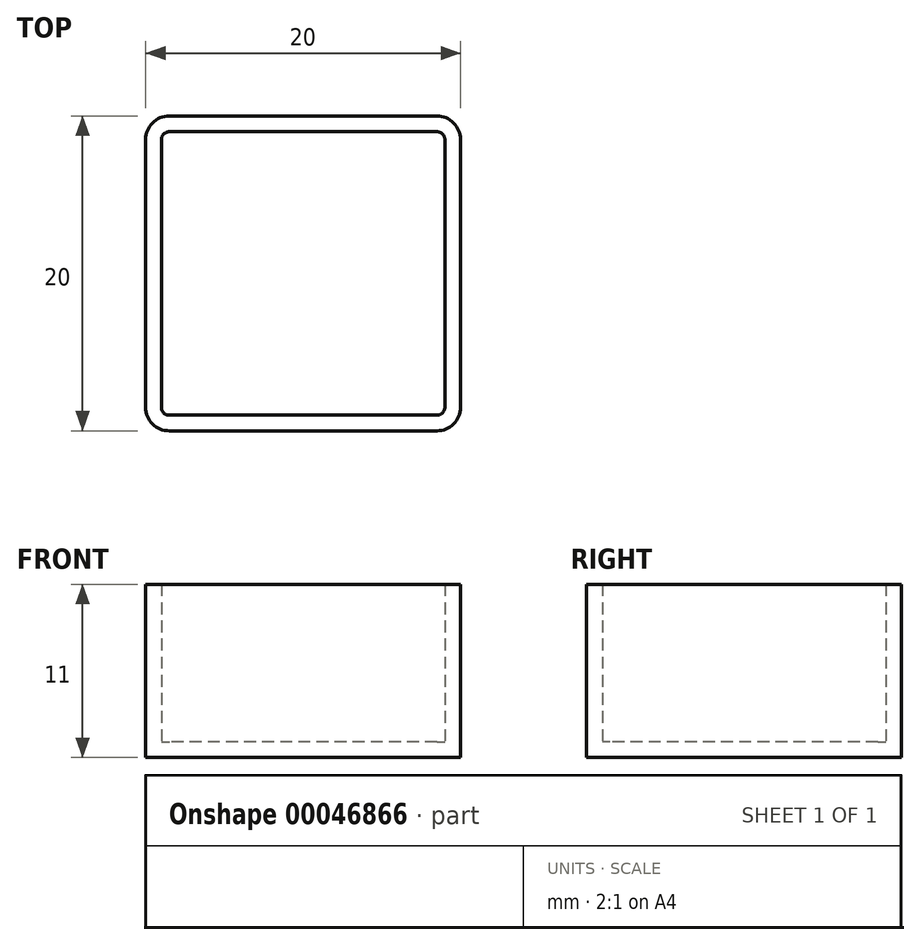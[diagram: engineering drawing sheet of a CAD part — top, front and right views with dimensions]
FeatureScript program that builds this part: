
annotation { "Feature Type Name" : "Feature", "Feature Type Description" : "" }
export const myFeature = defineFeature(function(context is Context, id is Id, definition is map)
    precondition{}
    {
        {
            var Q0;
            Q0=qCreatedBy(makeId("Top.planeOp"),FACE);
            var sketch = newSketch(context, id + "F0", { "sketchPlane" : qUnion([Q0])});
            skLineSegment(sketch, "E0.rect.bottom", {"start": v(10, 10) * mm, "end": v(-10, 10) * mm});
            skLineSegment(sketch, "E0.rect.top", {"start": v(10, -10) * mm, "end": v(-10, -10) * mm});
            skLineSegment(sketch, "E0.rect.left", {"start": v(10, 10) * mm, "end": v(10, -10) * mm});
            skLineSegment(sketch, "E0.rect.right", {"start": v(-10, 10) * mm, "end": v(-10, -10) * mm});
            skPoint(sketch, "E0.rect.middle", {"position": v(0, 0) * mm});
            skSolve(sketch);
        }
        {
            var Q0;
            Q0=makeQuery(id+"F0.imprint","IMPRINT",FACE,{"disambiguationData":[TD([[makeQuery(id+"F0.imprint","IMPRINT",EDGE,{"derivedFrom":sQuery(id+"F0.wireOp",EDGE,"E0.rect.bottom")}),1.0]])]});
            extrude(context, id + "F1", {"entities" : qUnion([Q0]), "depth" : 1 * mm});
        }
        {
            var Q0;
            Q0=makeQuery(id+"F1.opExtrude","CAP_FACE",FACE,{"disambiguationData":[OSD([sQuery(id+"F0.wireOp",EDGE,"E0.rect.bottom"),sQuery(id+"F0.wireOp",EDGE,"E0.rect.top"),sQuery(id+"F0.wireOp",EDGE,"E0.rect.left"),sQuery(id+"F0.wireOp",EDGE,"E0.rect.right")])],"isStart":false});
            var sketch = newSketch(context, id + "F2", { "sketchPlane" : qUnion([Q0])});
            skLineSegment(sketch, "E1.rect.bottom", {"start": v(9, 9) * mm, "end": v(-9, 9) * mm});
            skLineSegment(sketch, "E1.rect.top", {"start": v(9, -9) * mm, "end": v(-9, -9) * mm});
            skLineSegment(sketch, "E1.rect.left", {"start": v(9, 9) * mm, "end": v(9, -9) * mm});
            skLineSegment(sketch, "E1.rect.right", {"start": v(-9, 9) * mm, "end": v(-9, -9) * mm});
            skPoint(sketch, "E1.rect.middle", {"position": v(0, 0) * mm});
            skSolve(sketch);
        }
        {
            var Q0;
            Q0=makeQuery(id+"F2.imprint","IMPRINT",FACE,{"disambiguationData":[TD([[makeQuery(id+"F2.imprint","IMPRINT",EDGE,{"derivedFrom":sQuery(id+"F2.wireOp",EDGE,"E1.rect.bottom")}),-1.0]])]});
            extrude(context, id + "F3", {"entities" : qUnion([Q0]), "operationType" : NewBodyOperationType.ADD, "depth" : 10 * mm});
        }
        {
            var Q0;
            {var subQ0=sQuery(id+"F0.wireOp",EDGE,"E0.rect.top");var subQ1=sQuery(id+"F0.wireOp",EDGE,"E0.rect.left");Q0=makeQuery(id+"F3.boolean.opBoolean","MERGE",EDGE,{"derivedFrom":[makeQuery(id+"F1.opExtrude","SWEPT_EDGE",EDGE,{"disambiguationData":[OSD([subQ0,subQ1])]}),makeQuery(id+"F3.opExtrude","SWEPT_EDGE",EDGE,{"disambiguationData":[OSD([subQ0,subQ1])]})]});}
            fillet(context, id + "F4", {"entities" : qUnion([Q0]), "radius" : 1.5 * mm, "tangentPropagation" : true, "allowEdgeOverflow" : false});
        }
        {
            var Q0;
            Q0=makeQuery(id+"F3.opExtrude","SWEPT_EDGE",EDGE,{"disambiguationData":[OSD([sQuery(id+"F2.wireOp",EDGE,"E1.rect.top"),sQuery(id+"F2.wireOp",EDGE,"E1.rect.left")])]});
            fillet(context, id + "F5", {"entities" : qUnion([Q0]), "radius" : 0.5 * mm, "tangentPropagation" : true, "allowEdgeOverflow" : false});
        }
        {
            var Q0;
            {var subQ0=sQuery(id+"F0.wireOp",EDGE,"E0.rect.bottom");var subQ1=sQuery(id+"F0.wireOp",EDGE,"E0.rect.left");Q0=makeQuery(id+"F3.boolean.opBoolean","MERGE",EDGE,{"derivedFrom":[makeQuery(id+"F1.opExtrude","SWEPT_EDGE",EDGE,{"disambiguationData":[OSD([subQ0,subQ1])]}),makeQuery(id+"F3.opExtrude","SWEPT_EDGE",EDGE,{"disambiguationData":[OSD([subQ0,subQ1])]})]});}
            fillet(context, id + "F6", {"entities" : qUnion([Q0]), "radius" : 1.5 * mm, "tangentPropagation" : true, "allowEdgeOverflow" : false});
        }
        {
            var Q0;
            {var subQ0=sQuery(id+"F0.wireOp",EDGE,"E0.rect.bottom");var subQ1=sQuery(id+"F0.wireOp",EDGE,"E0.rect.right");Q0=makeQuery(id+"F3.boolean.opBoolean","MERGE",EDGE,{"derivedFrom":[makeQuery(id+"F1.opExtrude","SWEPT_EDGE",EDGE,{"disambiguationData":[OSD([subQ0,subQ1])]}),makeQuery(id+"F3.opExtrude","SWEPT_EDGE",EDGE,{"disambiguationData":[OSD([subQ0,subQ1])]})]});}
            fillet(context, id + "F7", {"entities" : qUnion([Q0]), "radius" : 1.5 * mm, "tangentPropagation" : true, "allowEdgeOverflow" : false});
        }
        {
            var Q0;
            {var subQ0=sQuery(id+"F0.wireOp",EDGE,"E0.rect.top");var subQ1=sQuery(id+"F0.wireOp",EDGE,"E0.rect.right");Q0=makeQuery(id+"F3.boolean.opBoolean","MERGE",EDGE,{"derivedFrom":[makeQuery(id+"F1.opExtrude","SWEPT_EDGE",EDGE,{"disambiguationData":[OSD([subQ0,subQ1])]}),makeQuery(id+"F3.opExtrude","SWEPT_EDGE",EDGE,{"disambiguationData":[OSD([subQ0,subQ1])]})]});}
            fillet(context, id + "F8", {"entities" : qUnion([Q0]), "radius" : 1.5 * mm, "tangentPropagation" : true, "allowEdgeOverflow" : false});
        }
        {
            var Q0;
            Q0=makeQuery(id+"F3.opExtrude","SWEPT_EDGE",EDGE,{"disambiguationData":[OSD([sQuery(id+"F2.wireOp",EDGE,"E1.rect.bottom"),sQuery(id+"F2.wireOp",EDGE,"E1.rect.right")])]});
            fillet(context, id + "F9", {"entities" : qUnion([Q0]), "radius" : 0.5 * mm, "tangentPropagation" : true, "allowEdgeOverflow" : false});
        }
        {
            var Q0;
            Q0=makeQuery(id+"F3.opExtrude","SWEPT_EDGE",EDGE,{"disambiguationData":[OSD([sQuery(id+"F2.wireOp",EDGE,"E1.rect.bottom"),sQuery(id+"F2.wireOp",EDGE,"E1.rect.left")])]});
            fillet(context, id + "F10", {"entities" : qUnion([Q0]), "radius" : 0.5 * mm, "tangentPropagation" : true, "allowEdgeOverflow" : false});
        }
        {
            var Q0;
            Q0=makeQuery(id+"F3.opExtrude","SWEPT_EDGE",EDGE,{"disambiguationData":[OSD([sQuery(id+"F2.wireOp",EDGE,"E1.rect.top"),sQuery(id+"F2.wireOp",EDGE,"E1.rect.right")])]});
            fillet(context, id + "F11", {"entities" : qUnion([Q0]), "radius" : 0.5 * mm, "tangentPropagation" : true, "allowEdgeOverflow" : false});
        }
    });
